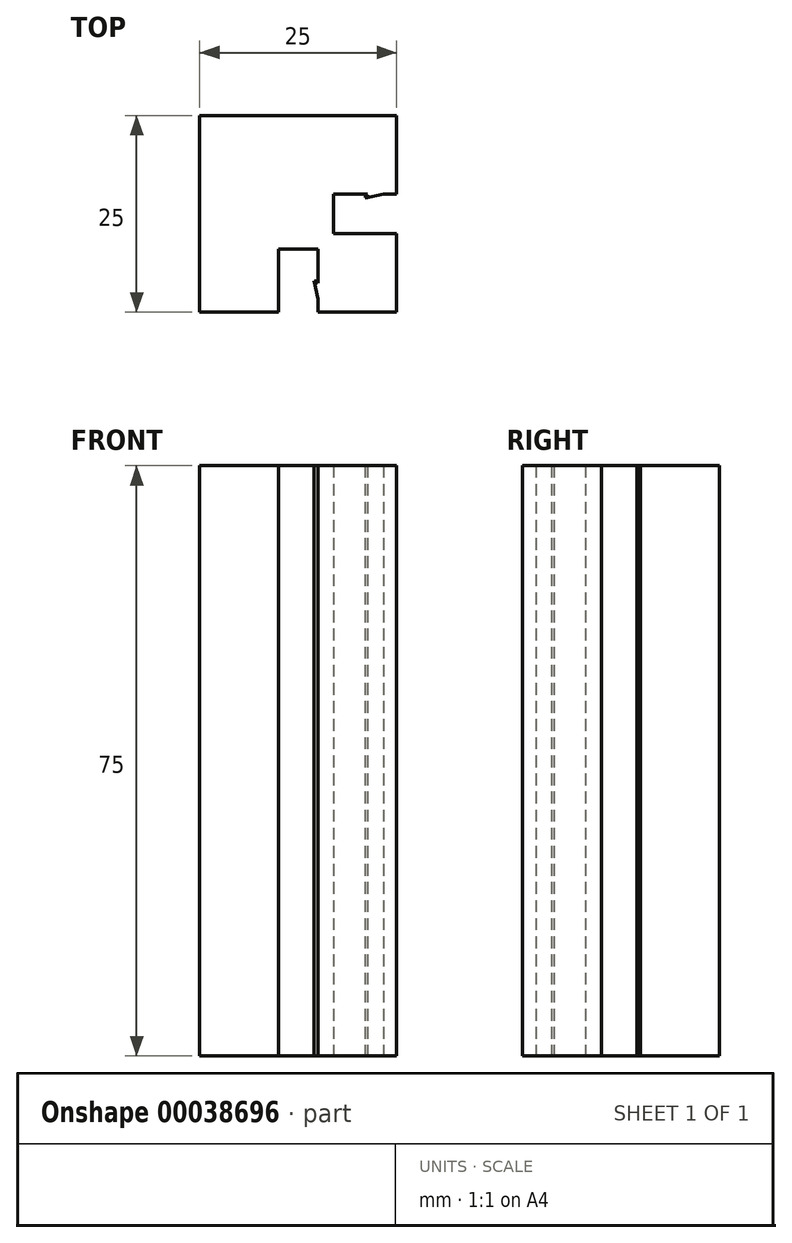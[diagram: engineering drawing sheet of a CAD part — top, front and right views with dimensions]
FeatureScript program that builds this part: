
annotation { "Feature Type Name" : "Feature", "Feature Type Description" : "" }
export const myFeature = defineFeature(function(context is Context, id is Id, definition is map)
    precondition{}
    {
        {
            var Q0;
            Q0=qCreatedBy(makeId("Top.planeOp"),FACE);
            var sketch = newSketch(context, id + "F0", { "sketchPlane" : qUnion([Q0])});
            skLineSegment(sketch, "E0.rect.bottom", {"start": v(12.5, -12.5) * mm, "end": v(-12.5, -12.5) * mm});
            skLineSegment(sketch, "E0.rect.top", {"start": v(12.5, 12.5) * mm, "end": v(-12.5, 12.5) * mm});
            skLineSegment(sketch, "E0.rect.left", {"start": v(12.5, -12.5) * mm, "end": v(12.5, 12.5) * mm});
            skLineSegment(sketch, "E0.rect.right", {"start": v(-12.5, -12.5) * mm, "end": v(-12.5, 12.5) * mm});
            skPoint(sketch, "E0.rect.middle", {"position": v(0, 0) * mm});
            skLineSegment(sketch, "E1.rect.bottom", {"start": v(2.5, -4.5) * mm, "end": v(-2.5, -4.5) * mm});
            skLineSegment(sketch, "E1.rect.top", {"start": v(2.5, -20.5) * mm, "end": v(-2.5, -20.5) * mm});
            skLineSegment(sketch, "E1.rect.left", {"start": v(2.5, -4.5) * mm, "end": v(2.5, -8.82) * mm});
            skLineSegment(sketch, "E1.rect.right", {"start": v(-2.5, -4.5) * mm, "end": v(-2.5, -20.5) * mm});
            skPoint(sketch, "E1.rect.middle", {"position": v(0, -12.5) * mm});
            skLineSegment(sketch, "E2.rect.bottom", {"start": v(4.5, 2.5) * mm, "end": v(8.82, 2.5) * mm});
            skLineSegment(sketch, "E2.rect.top", {"start": v(4.5, -2.5) * mm, "end": v(20.5, -2.5) * mm});
            skLineSegment(sketch, "E2.rect.left", {"start": v(4.5, 2.5) * mm, "end": v(4.5, -2.5) * mm});
            skLineSegment(sketch, "E2.rect.right", {"start": v(20.5, 2.5) * mm, "end": v(20.5, -2.5) * mm});
            skPoint(sketch, "E2.rect.middle", {"position": v(12.5, 0) * mm});
            skLineSegment(sketch, "E3", {"start": v(2.5, -8.82) * mm, "end": v(2, -8.5) * mm});
            skLineSegment(sketch, "E4", {"start": v(2, -8.5) * mm, "end": v(2.5, -10.82) * mm});
            skLineSegment(sketch, "E5", {"start": v(8.82, 2.5) * mm, "end": v(8.5, 2) * mm});
            skLineSegment(sketch, "E6", {"start": v(8.5, 2) * mm, "end": v(10.82, 2.5) * mm});
            skLineSegment(sketch, "E7.trimOffspring", {"start": v(10.82, 2.5) * mm, "end": v(20.5, 2.5) * mm});
            skLineSegment(sketch, "E8.trimOffspring", {"start": v(2.5, -10.82) * mm, "end": v(2.5, -20.5) * mm});
            skSolve(sketch);
        }
        {
            var Q0;
            {var subQ10=sQuery(id+"F0.wireOp",EDGE,"E0.rect.top");Q0=makeQuery(id+"F0.imprint","IMPRINT",FACE,{"disambiguationData":[TD([[makeQuery(id+"F0.imprint","IMPRINT",EDGE,{"derivedFrom":subQ10}),1.0]])]});}
            extrude(context, id + "F1", {"entities" : qUnion([Q0]), "depth" : 75 * mm});
        }
    });
